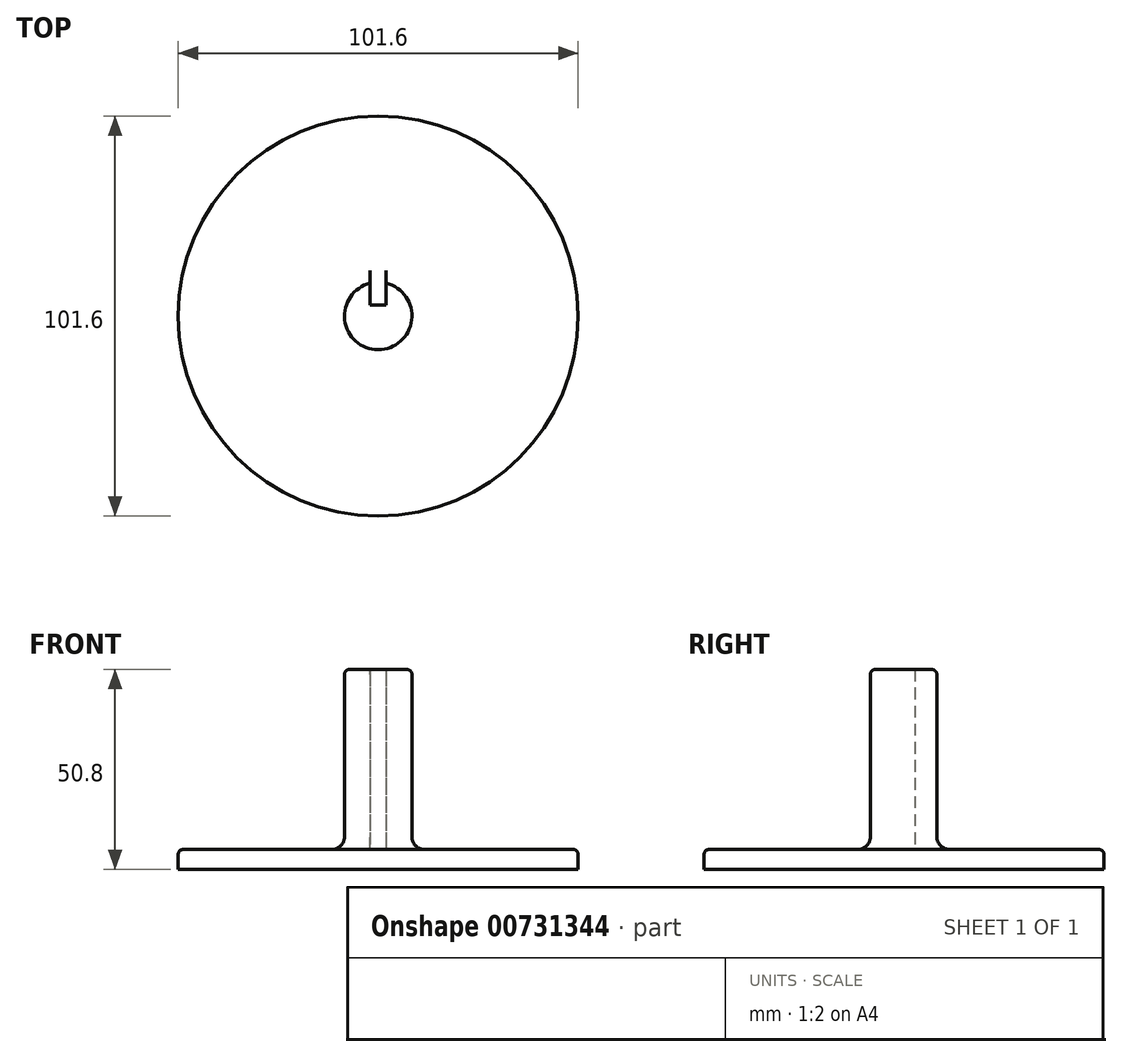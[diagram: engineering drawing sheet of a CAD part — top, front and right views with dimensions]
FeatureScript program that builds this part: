
annotation { "Feature Type Name" : "Feature", "Feature Type Description" : "" }
export const myFeature = defineFeature(function(context is Context, id is Id, definition is map)
    precondition{}
    {
        {
            var Q0;
            Q0=qCreatedBy(makeId("Top.planeOp"),FACE);
            var sketch = newSketch(context, id + "F0", { "sketchPlane" : qUnion([Q0])});
            skCircle(sketch, "E0", {"center": v(0, 0) * mm, "radius": 50.8 * mm});
            skSolve(sketch);
        }
        {
            var Q0;
            Q0=qCreatedBy(makeId("Top.planeOp"),FACE);
            var sketch = newSketch(context, id + "F1", { "sketchPlane" : qUnion([Q0])});
            skCircle(sketch, "E1", {"center": v(0, 0) * mm, "radius": 8.57 * mm});
            skPoint(sketch, "E2", {"position": v(-2.03, 8.33) * mm});
            skPoint(sketch, "E3", {"position": v(2.03, 8.33) * mm});
            skPoint(sketch, "E4", {"position": v(-2.03, 2.74) * mm});
            skPoint(sketch, "E5", {"position": v(2.03, 2.74) * mm});
            skLineSegment(sketch, "E6", {"start": v(-2.03, 2.74) * mm, "end": v(2.03, 2.74) * mm});
            skLineSegment(sketch, "E7", {"start": v(-2.03, 8.33) * mm, "end": v(-2.03, 2.74) * mm});
            skLineSegment(sketch, "E8", {"start": v(2.03, 8.33) * mm, "end": v(2.03, 2.74) * mm});
            skPoint(sketch, "E9", {"position": v(0, 2.74) * mm});
            skSolve(sketch);
        }
        {
            var Q0;
            Q0=makeQuery(id+"F1.imprint","IMPRINT",FACE,{"disambiguationData":[TD([[makeQuery(id+"F1.imprint","IMPRINT",EDGE,{"derivedFrom":sQuery(id+"F1.wireOp",EDGE,"E6")}),-1.0]])]});
            extrude(context, id + "F2", {"entities" : qUnion([Q0]), "depth" : 50.8 * mm, "offsetDistance" : 25.4 * mm});
        }
        {
            var Q0;
            Q0 = qSketchRegion(id + "F0", true);
            extrude(context, id + "F3", {"entities" : qUnion([Q0]), "operationType" : NewBodyOperationType.ADD, "depth" : 5.08 * mm, "offsetDistance" : 25.4 * mm});
        }
        {
            var Q0;
            Q0=makeQuery(id+"F3.boolean.opBoolean","INTERSECT",EDGE,{"derivedFrom":[makeQuery(id+"F2.opExtrude","SWEPT_FACE",FACE,{"disambiguationData":[OSD([sQuery(id+"F1.wireOp",EDGE,"E1")])]}),makeQuery(id+"F3.opExtrude","CAP_FACE",FACE,{"disambiguationData":[OSD([sQuery(id+"F0.wireOp",EDGE,"E0")])],"isStart":false})]});
            fillet(context, id + "F4", {"entities" : qUnion([Q0]), "radius" : 3.17 * mm, "tangentPropagation" : true, "allowEdgeOverflow" : false});
        }
        {
            var Q0;
            Q0=makeQuery(id+"F2.opExtrude","CAP_EDGE",EDGE,{"disambiguationData":[OSD([sQuery(id+"F1.wireOp",EDGE,"E1")])],"isStart":false});
            var Q1;
            Q1=makeQuery(id+"F3.opExtrude","CAP_EDGE",EDGE,{"disambiguationData":[OSD([sQuery(id+"F0.wireOp",EDGE,"E0")])],"isStart":false});
            fillet(context, id + "F5", {"entities" : qUnion([Q0, Q1]), "radius" : 1.27 * mm, "tangentPropagation" : true, "allowEdgeOverflow" : false});
        }
    });
